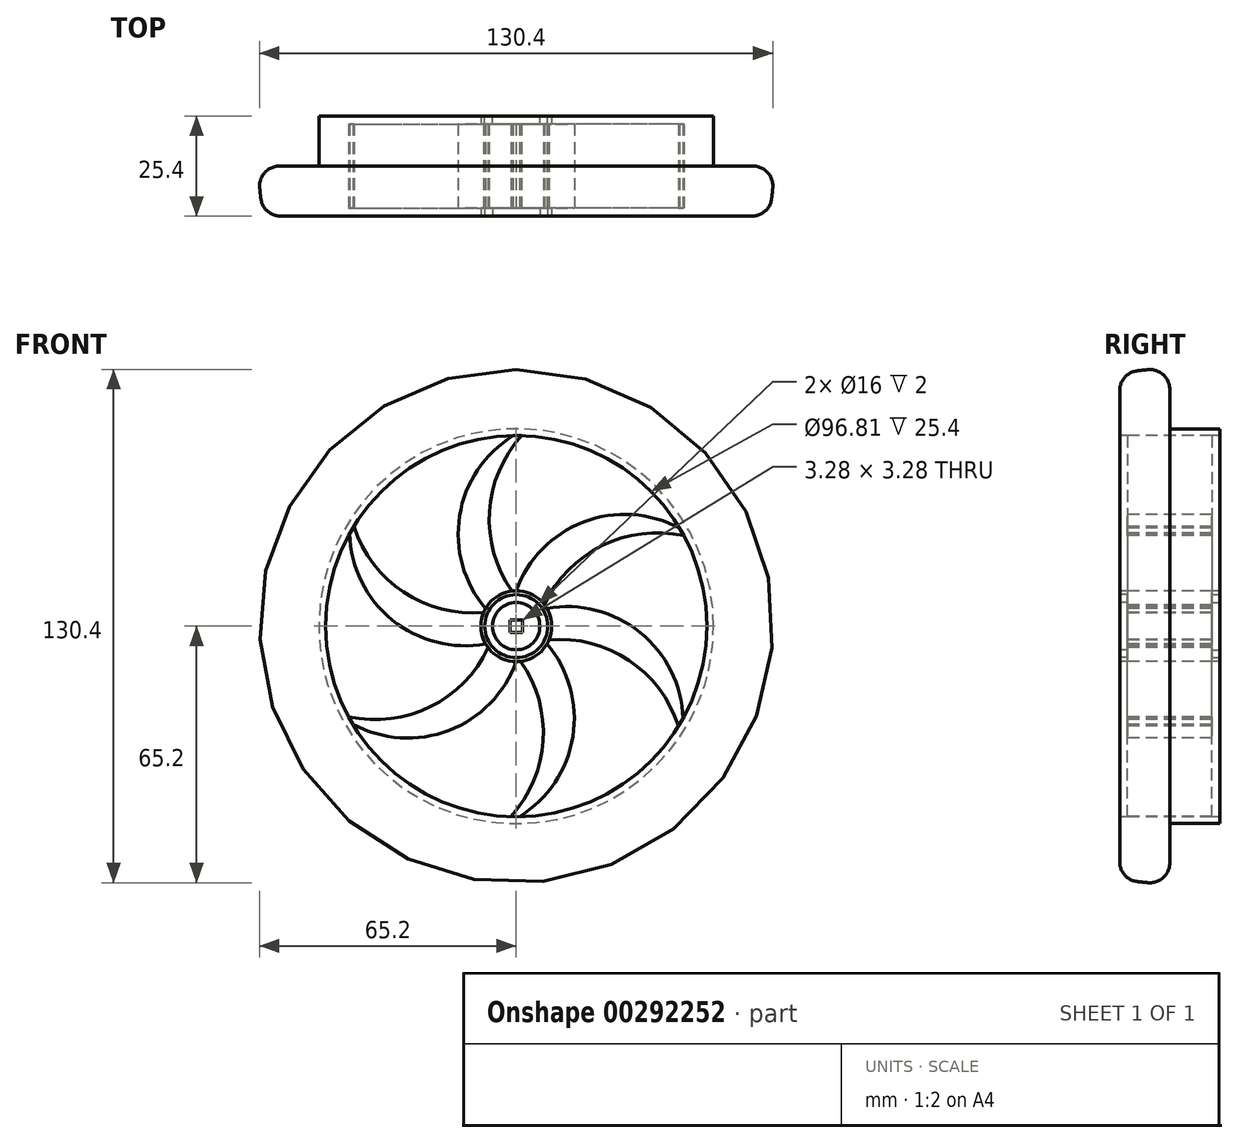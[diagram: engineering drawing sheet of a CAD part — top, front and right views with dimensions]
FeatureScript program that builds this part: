
annotation { "Feature Type Name" : "Feature", "Feature Type Description" : "" }
export const myFeature = defineFeature(function(context is Context, id is Id, definition is map)
    precondition{}
    {
        {
            var Q0;
            Q0=qCreatedBy(makeId("Top.planeOp"),FACE);
            var sketch = newSketch(context, id + "F0", { "sketchPlane" : qUnion([Q0])});
            skCircle(sketch, "E0", {"center": v(0, 0) * mm, "radius": 65.4 * mm});
            skLineSegment(sketch, "E1", {"start": v(0, 0) * mm, "end": v(0, -12.7) * mm});
            skLineSegment(sketch, "E2", {"start": v(0, -12.7) * mm, "end": v(64.16, -12.7) * mm});
            skLineSegment(sketch, "E3", {"start": v(0, 0) * mm, "end": v(0, 12.7) * mm});
            skLineSegment(sketch, "E4", {"start": v(50.16, 12.7) * mm, "end": v(64.16, 12.7) * mm});
            skLineSegment(sketch, "E5", {"start": v(64.16, 12.7) * mm, "end": v(50.16, 12.7) * mm});
            skLineSegment(sketch, "E6", {"start": v(50.16, 12.7) * mm, "end": v(50.16, -12.7) * mm});
            skLineSegment(sketch, "E7", {"start": v(0, 0) * mm, "end": v(65.4, 0) * mm});
            skSolve(sketch);
        }
        {
            var Q0;
            {var subQ3=sQuery(id+"F0.wireOp",EDGE,"E5");Q0=makeQuery(id+"F0.imprint","IMPRINT",FACE,{"disambiguationData":[TD([[makeQuery(id+"F0.imprint","IMPRINT",EDGE,{"derivedFrom":subQ3}),1.0]])]});}
            var Q1;
            {var subQ0=sQuery(id+"F0.wireOp",EDGE,"E2");var subQ1=sQuery(id+"F0.wireOp",EDGE,"E0");var subQ2=makeQuery(id+"F0.imprint","INTERSECT",VERTEX,{"derivedFrom":[subQ1,subQ0]});Q1=makeQuery(id+"F0.imprint","IMPRINT",FACE,{"disambiguationData":[TD([[makeQuery(id+"F0.imprint","IMPRINT",EDGE,{"disambiguationData":[TD([[subQ2,-1.0]])],"derivedFrom":subQ1}),1.0]])]});}
            var Q2;
            Q2=sQuery(id+"F0.wireOp",EDGE,"E1");
            revolve(context, id + "F1", {"entities" : qUnion([Q0, Q1]), "axis" : qUnion([Q2]), "revolveType" : RevolveType.FULL});
        }
        {
            var Q0;
            Q0=makeQuery(id+"F1.opRevolve","SWEPT_EDGE",EDGE,{"disambiguationData":[OSD([sQuery(id+"F0.wireOp",EDGE,"E0"),sQuery(id+"F0.wireOp",EDGE,"E2")])]});
            var Q1;
            Q1=makeQuery(id+"F1.opRevolve","SWEPT_EDGE",EDGE,{"disambiguationData":[OSD([sQuery(id+"F0.wireOp",EDGE,"E0"),sQuery(id+"F0.wireOp",EDGE,"E5")])]});
            fillet(context, id + "F2", {"entities" : qUnion([Q0, Q1]), "radius" : 5 * mm, "tangentPropagation" : true, "allowEdgeOverflow" : false});
        }
        {
            var Q0;
            {var subQ1=sQuery(id+"F0.wireOp",EDGE,"E1");Q0=makeQuery(id+"F0.imprint","IMPRINT",FACE,{"disambiguationData":[TD([[makeQuery(id+"F0.imprint","IMPRINT",EDGE,{"derivedFrom":subQ1}),1.0]])]});}
            var Q1;
            Q1=sQuery(id+"F0.wireOp",EDGE,"E1");
            revolve(context, id + "F3", {"entities" : qUnion([Q0]), "axis" : qUnion([Q1]), "revolveType" : RevolveType.FULL});
        }
        {
            var Q0;
            Q0=makeQuery(id+"F3.opRevolve","SWEPT_FACE",FACE,{"disambiguationData":[OSD([sQuery(id+"F0.wireOp",EDGE,"E2")])]});
            var sketch = newSketch(context, id + "F4", { "sketchPlane" : qUnion([Q0])});
            skLineSegment(sketch, "E8.bottom", {"start": v(1.64, -1.64) * mm, "end": v(-1.64, -1.64) * mm});
            skLineSegment(sketch, "E8.top", {"start": v(1.64, 1.64) * mm, "end": v(-1.64, 1.64) * mm});
            skLineSegment(sketch, "E8.left", {"start": v(1.64, -1.64) * mm, "end": v(1.64, 1.64) * mm});
            skLineSegment(sketch, "E8.right", {"start": v(-1.64, -1.64) * mm, "end": v(-1.64, 1.64) * mm});
            skPoint(sketch, "E8.middle", {"position": v(0, 0) * mm});
            skCircle(sketch, "E9", {"center": v(0, 0) * mm, "radius": 48.4 * mm});
            skCircle(sketch, "E10", {"center": v(0, 0) * mm, "radius": 6 * mm});
            skCircle(sketch, "E11", {"center": v(0, 0) * mm, "radius": 8 * mm});
            skCircle(sketch, "E12", {"center": v(0, 0) * mm, "radius": 9 * mm});
            skArc(sketch, "E13", {"start": v(41.5, 24.9) * mm, "mid": v(17.1, 26.48) * mm, "end": v(0, 9) * mm});
            skArc(sketch, "E14", {"start": v(42.6, 23) * mm, "mid": v(21.8, 20.45) * mm, "end": v(7.16, 5.45) * mm});
            skArc(sketch, "E15.1.0", {"start": v(1.38, 48.38) * mm, "mid": v(-6.82, 29.1) * mm, "end": v(-1.14, 8.93) * mm});
            skArc(sketch, "E15.1.1", {"start": v(-0.8, 48.4) * mm, "mid": v(-14.38, 28.05) * mm, "end": v(-7.8, 4.5) * mm});
            skArc(sketch, "E15.2.0", {"start": v(-41.21, 25.39) * mm, "mid": v(-28.6, 8.65) * mm, "end": v(-8.3, 3.48) * mm});
            skArc(sketch, "E15.2.1", {"start": v(-42.32, 23.5) * mm, "mid": v(-31.49, 1.57) * mm, "end": v(-7.8, -4.5) * mm});
            skArc(sketch, "E15.3.0", {"start": v(-42.6, -23) * mm, "mid": v(-21.8, -20.45) * mm, "end": v(-7.16, -5.45) * mm});
            skArc(sketch, "E15.3.1", {"start": v(-41.5, -24.9) * mm, "mid": v(-17.1, -26.48) * mm, "end": v(0, -9) * mm});
            skArc(sketch, "E15.4.0", {"start": v(-1.38, -48.38) * mm, "mid": v(6.82, -29.1) * mm, "end": v(1.14, -8.93) * mm});
            skArc(sketch, "E15.4.1", {"start": v(0.8, -48.4) * mm, "mid": v(14.38, -28.05) * mm, "end": v(7.8, -4.5) * mm});
            skArc(sketch, "E15.5.0", {"start": v(41.21, -25.39) * mm, "mid": v(28.6, -8.65) * mm, "end": v(8.3, -3.48) * mm});
            skArc(sketch, "E15.5.1", {"start": v(42.32, -23.5) * mm, "mid": v(31.49, -1.57) * mm, "end": v(7.8, 4.5) * mm});
            skSolve(sketch);
        }
        {
            var Q0;
            {var subQ0=sQuery(id+"F4.wireOp",EDGE,"E14");Q0=makeQuery(id+"F4.imprint","IMPRINT",FACE,{"disambiguationData":[TD([[makeQuery(id+"F4.imprint","IMPRINT",EDGE,{"derivedFrom":subQ0}),1.0]])]});}
            var Q1;
            {var subQ0=sQuery(id+"F4.wireOp",EDGE,"E13");Q1=makeQuery(id+"F4.imprint","IMPRINT",FACE,{"disambiguationData":[TD([[makeQuery(id+"F4.imprint","IMPRINT",EDGE,{"derivedFrom":subQ0}),-1.0]])]});}
            var Q2;
            {var subQ0=sQuery(id+"F4.wireOp",EDGE,"E15.1.1");Q2=makeQuery(id+"F4.imprint","IMPRINT",FACE,{"disambiguationData":[TD([[makeQuery(id+"F4.imprint","IMPRINT",EDGE,{"derivedFrom":subQ0}),-1.0]])]});}
            var Q3;
            {var subQ0=sQuery(id+"F4.wireOp",EDGE,"E15.2.1");Q3=makeQuery(id+"F4.imprint","IMPRINT",FACE,{"disambiguationData":[TD([[makeQuery(id+"F4.imprint","IMPRINT",EDGE,{"derivedFrom":subQ0}),-1.0]])]});}
            var Q4;
            {var subQ0=sQuery(id+"F4.wireOp",EDGE,"E15.3.1");Q4=makeQuery(id+"F4.imprint","IMPRINT",FACE,{"disambiguationData":[TD([[makeQuery(id+"F4.imprint","IMPRINT",EDGE,{"derivedFrom":subQ0}),-1.0]])]});}
            var Q5;
            {var subQ0=sQuery(id+"F4.wireOp",EDGE,"E15.4.1");Q5=makeQuery(id+"F4.imprint","IMPRINT",FACE,{"disambiguationData":[TD([[makeQuery(id+"F4.imprint","IMPRINT",EDGE,{"derivedFrom":subQ0}),-1.0]])]});}
            var Q6;
            Q6=makeQuery(id+"F4.imprint","IMPRINT",FACE,{"disambiguationData":[TD([[makeQuery(id+"F4.imprint","IMPRINT",EDGE,{"derivedFrom":sQuery(id+"F4.wireOp",EDGE,"E8.bottom")}),-1.0]])]});
            extrude(context, id + "F5", {"entities" : qUnion([Q0, Q1, Q2, Q3, Q4, Q5, Q6]), "operationType" : NewBodyOperationType.REMOVE, "oppositeDirection" : true, "depth" : 500 * mm});
        }
        {
            var Q0;
            Q0=makeQuery(id+"F4.imprint","IMPRINT",FACE,{"disambiguationData":[TD([[makeQuery(id+"F4.imprint","IMPRINT",EDGE,{"derivedFrom":sQuery(id+"F4.wireOp",EDGE,"E10")}),-1.0]])]});
            var Q1;
            {var subQ0=sQuery(id+"F4.wireOp",EDGE,"E15.1.0");Q1=makeQuery(id+"F4.imprint","IMPRINT",FACE,{"disambiguationData":[TD([[makeQuery(id+"F4.imprint","IMPRINT",EDGE,{"derivedFrom":subQ0}),-1.0]])]});}
            var Q2;
            {var subQ0=sQuery(id+"F4.wireOp",EDGE,"E15.2.0");Q2=makeQuery(id+"F4.imprint","IMPRINT",FACE,{"disambiguationData":[TD([[makeQuery(id+"F4.imprint","IMPRINT",EDGE,{"derivedFrom":subQ0}),-1.0]])]});}
            var Q3;
            {var subQ0=sQuery(id+"F4.wireOp",EDGE,"E15.3.0");Q3=makeQuery(id+"F4.imprint","IMPRINT",FACE,{"disambiguationData":[TD([[makeQuery(id+"F4.imprint","IMPRINT",EDGE,{"derivedFrom":subQ0}),-1.0]])]});}
            var Q4;
            {var subQ0=sQuery(id+"F4.wireOp",EDGE,"E15.4.0");Q4=makeQuery(id+"F4.imprint","IMPRINT",FACE,{"disambiguationData":[TD([[makeQuery(id+"F4.imprint","IMPRINT",EDGE,{"derivedFrom":subQ0}),-1.0]])]});}
            var Q5;
            {var subQ0=sQuery(id+"F4.wireOp",EDGE,"E15.5.0");Q5=makeQuery(id+"F4.imprint","IMPRINT",FACE,{"disambiguationData":[TD([[makeQuery(id+"F4.imprint","IMPRINT",EDGE,{"derivedFrom":subQ0}),-1.0]])]});}
            var Q6;
            {var subQ0=sQuery(id+"F4.wireOp",EDGE,"E13");Q6=makeQuery(id+"F4.imprint","IMPRINT",FACE,{"disambiguationData":[TD([[makeQuery(id+"F4.imprint","IMPRINT",EDGE,{"derivedFrom":subQ0}),1.0]])]});}
            extrude(context, id + "F6", {"entities" : qUnion([Q0, Q1, Q2, Q3, Q4, Q5, Q6]), "operationType" : NewBodyOperationType.REMOVE, "oppositeDirection" : true, "depth" : 2 * mm});
        }
        {
            var Q0;
            Q0=makeQuery(id+"F3.opRevolve","SWEPT_BODY",BODY,{"disambiguationData":[OSD([sQuery(id+"F0.wireOp",EDGE,"E1"),sQuery(id+"F0.wireOp",EDGE,"E2"),sQuery(id+"F0.wireOp",EDGE,"E6"),sQuery(id+"F0.wireOp",EDGE,"E7")])]});
            var Q1;
            Q1=qCreatedBy(makeId("Front.planeOp"),FACE);
            mirror(context, id + "F7", {"operationType" : NewBodyOperationType.ADD, "entities" : qUnion([Q0]), "mirrorPlane" : qUnion([Q1])});
        }
    });
